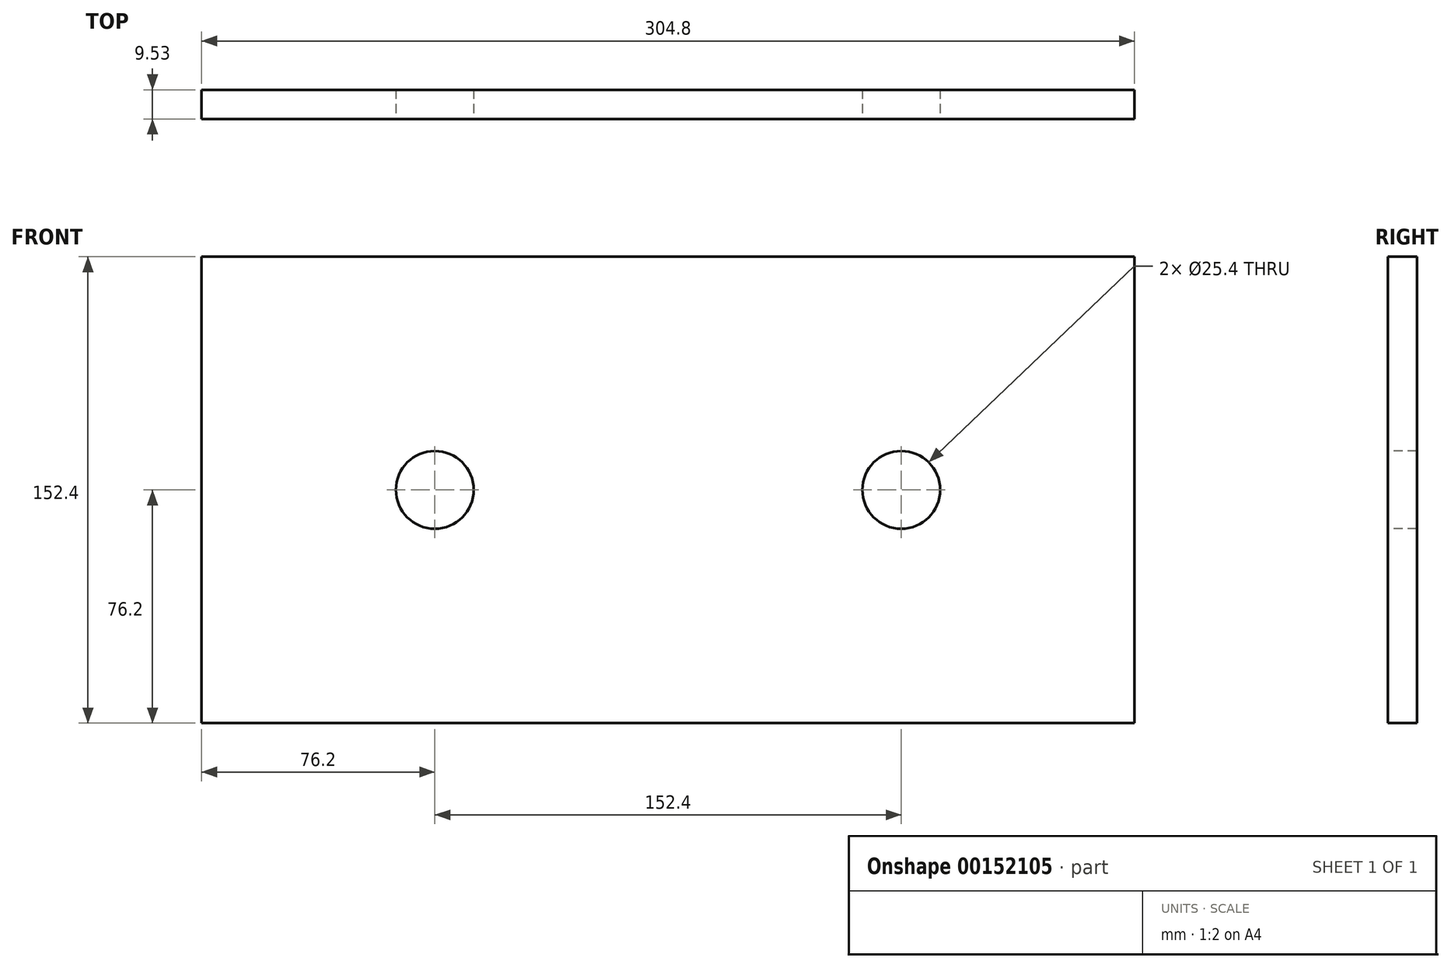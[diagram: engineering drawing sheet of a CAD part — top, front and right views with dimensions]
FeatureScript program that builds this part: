
annotation { "Feature Type Name" : "Feature", "Feature Type Description" : "" }
export const myFeature = defineFeature(function(context is Context, id is Id, definition is map)
    precondition{}
    {
        {
            var Q0;
            Q0=qCreatedBy(makeId("Front.planeOp"),FACE);
            var sketch = newSketch(context, id + "F0", { "sketchPlane" : qUnion([Q0])});
            skLineSegment(sketch, "E0.bottom", {"start": v(0, 0) * mm, "end": v(-304.8, 0) * mm});
            skLineSegment(sketch, "E0.top", {"start": v(0, 152.4) * mm, "end": v(-304.8, 152.4) * mm});
            skLineSegment(sketch, "E0.left", {"start": v(0, 0) * mm, "end": v(0, 152.4) * mm});
            skLineSegment(sketch, "E0.right", {"start": v(-304.8, 0) * mm, "end": v(-304.8, 152.4) * mm});
            skSolve(sketch);
        }
        {
            var Q0;
            Q0=makeQuery(id+"F0.imprint","IMPRINT",FACE,{"disambiguationData":[TD([[makeQuery(id+"F0.imprint","IMPRINT",EDGE,{"derivedFrom":sQuery(id+"F0.wireOp",EDGE,"E0.bottom")}),-1.0]])]});
            extrude(context, id + "F1", {"entities" : qUnion([Q0]), "depth" : 9.52 * mm});
        }
        {
            var Q0;
            Q0=makeQuery(id+"F1.opExtrude","CAP_FACE",FACE,{"disambiguationData":[OSD([sQuery(id+"F0.wireOp",EDGE,"E0.bottom"),sQuery(id+"F0.wireOp",EDGE,"E0.top"),sQuery(id+"F0.wireOp",EDGE,"E0.left"),sQuery(id+"F0.wireOp",EDGE,"E0.right")])],"isStart":false});
            var sketch = newSketch(context, id + "F2", { "sketchPlane" : qUnion([Q0])});
            skCircle(sketch, "E1", {"center": v(-228.6, 76.2) * mm, "radius": 12.7 * mm});
            skCircle(sketch, "E2", {"center": v(-76.2, 76.2) * mm, "radius": 12.7 * mm});
            skLineSegment(sketch, "E3", {"start": v(-228.6, 76.2) * mm, "end": v(-76.2, 76.2) * mm, "construction": true});
            skPoint(sketch, "E4", {"position": v(-152.4, 152.4) * mm});
            skPoint(sketch, "E5", {"position": v(-152.4, 76.2) * mm});
            skPoint(sketch, "E6", {"position": v(-304.8, 76.2) * mm});
            skSolve(sketch);
        }
        {
            var Q0;
            Q0 = qSketchRegion(id + "F2", true);
            extrude(context, id + "F3", {"entities" : qUnion([Q0]), "operationType" : NewBodyOperationType.REMOVE, "endBound" : BoundingType.THROUGH_ALL, "oppositeDirection" : true, "depth" : 25.4 * mm});
        }
    });
